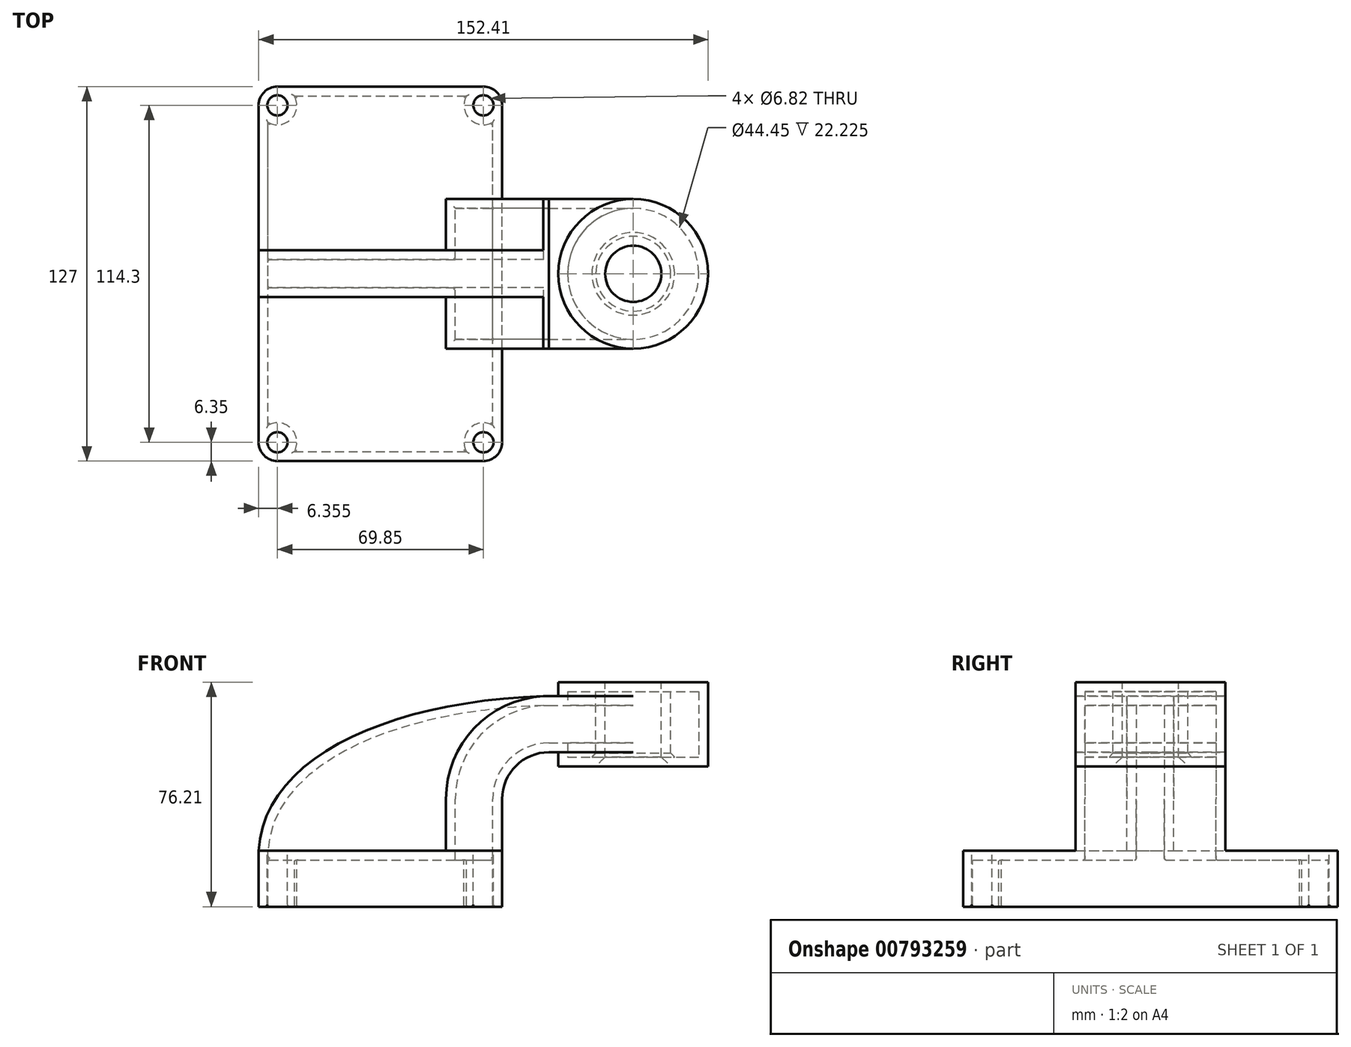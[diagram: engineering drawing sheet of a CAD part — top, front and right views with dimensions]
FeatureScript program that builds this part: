
annotation { "Feature Type Name" : "Feature", "Feature Type Description" : "" }
export const myFeature = defineFeature(function(context is Context, id is Id, definition is map)
    precondition{}
    {
        {
            var Q0;
            Q0=qCreatedBy(makeId("Front.planeOp"),FACE);
            var sketch = newSketch(context, id + "F0", { "sketchPlane" : qUnion([Q0])});
            skLineSegment(sketch, "E0.bottom", {"start": v(-41.28, -9.53) * mm, "end": v(41.28, -9.53) * mm});
            skLineSegment(sketch, "E0.top", {"start": v(-41.28, 9.53) * mm, "end": v(41.28, 9.53) * mm});
            skLineSegment(sketch, "E0.left", {"start": v(-41.28, -9.53) * mm, "end": v(-41.28, 9.53) * mm});
            skLineSegment(sketch, "E0.right", {"start": v(41.28, -9.53) * mm, "end": v(41.28, 9.53) * mm});
            skPoint(sketch, "E0.middle", {"position": v(0, 0) * mm});
            skLineSegment(sketch, "E1.bottom", {"start": v(60.32, 38.1) * mm, "end": v(111.12, 38.1) * mm});
            skLineSegment(sketch, "E1.top", {"start": v(60.32, 66.67) * mm, "end": v(111.12, 66.67) * mm});
            skLineSegment(sketch, "E1.left", {"start": v(60.32, 38.1) * mm, "end": v(60.32, 66.67) * mm});
            skLineSegment(sketch, "E1.right", {"start": v(111.12, 38.1) * mm, "end": v(111.12, 66.67) * mm});
            skPoint(sketch, "E1.middle", {"position": v(85.72, 52.39) * mm});
            skLineSegment(sketch, "E2", {"start": v(41.28, 9.53) * mm, "end": v(41.28, 27) * mm});
            skArc(sketch, "E3", {"start": v(41.27, 27) * mm, "mid": v(45.92, 38.23) * mm, "end": v(57.15, 42.88) * mm});
            skLineSegment(sketch, "E4", {"start": v(57.15, 42.88) * mm, "end": v(85.72, 42.88) * mm});
            skLineSegment(sketch, "E5.0", {"start": v(57.15, 61.93) * mm, "end": v(85.72, 61.93) * mm});
            skArc(sketch, "E5.1", {"start": v(22.22, 27) * mm, "mid": v(32.45, 51.7) * mm, "end": v(57.15, 61.93) * mm});
            skLineSegment(sketch, "E5.2", {"start": v(22.22, 9.53) * mm, "end": v(22.22, 27) * mm});
            skLineSegment(sketch, "E6", {"start": v(85.72, 38.1) * mm, "end": v(85.72, 66.67) * mm});
            skPoint(sketch, "E7.orphan", {"position": v(85.72, 42.88) * mm});
            skFitSpline(sketch, "E8", {"points": [v(-41.28, 9.53) * mm, v(57.15, 61.93) * mm], "startDerivative": vector(4.92, 96) * mm, "endDerivative": vector(159.26, 3.79) * mm});
            skSolve(sketch);
        }
        {
            var Q0;
            Q0=makeQuery(id+"F0.imprint","IMPRINT",FACE,{"disambiguationData":[TD([[makeQuery(id+"F0.imprint","IMPRINT",EDGE,{"derivedFrom":sQuery(id+"F0.wireOp",EDGE,"E0.bottom")}),1.0]])]});
            extrude(context, id + "F1", {"entities" : qUnion([Q0]), "depth" : 127 * mm, "offsetDistance" : 25.4 * mm, "symmetric" : true});
        }
        {
            var Q0;
            {var subQ1=sQuery(id+"F0.wireOp",EDGE,"E2");Q0=makeQuery(id+"F0.imprint","IMPRINT",FACE,{"disambiguationData":[TD([[makeQuery(id+"F0.imprint","IMPRINT",EDGE,{"derivedFrom":subQ1}),1.0]])]});}
            extrude(context, id + "F2", {"entities" : qUnion([Q0]), "operationType" : NewBodyOperationType.ADD, "depth" : 50.8 * mm, "offsetDistance" : 25.4 * mm, "symmetric" : true});
        }
        {
            var Q0;
            {var subQ3=sQuery(id+"F0.wireOp",EDGE,"E5.2");Q0=makeQuery(id+"F0.imprint","IMPRINT",FACE,{"disambiguationData":[TD([[makeQuery(id+"F0.imprint","IMPRINT",EDGE,{"derivedFrom":subQ3}),1.0]])]});}
            extrude(context, id + "F3", {"entities" : qUnion([Q0]), "operationType" : NewBodyOperationType.ADD, "depth" : 15.88 * mm, "offsetDistance" : 25.4 * mm, "symmetric" : true});
        }
        {
            var Q0;
            {var subQ0=sQuery(id+"F0.wireOp",EDGE,"E4");var subQ1=sQuery(id+"F0.wireOp",EDGE,"E1.left");var subQ2=makeQuery(id+"F0.imprint","INTERSECT",VERTEX,{"derivedFrom":[subQ1,subQ0]});Q0=makeQuery(id+"F0.imprint","IMPRINT",FACE,{"disambiguationData":[TD([[makeQuery(id+"F0.imprint","IMPRINT",EDGE,{"disambiguationData":[TD([[subQ2,-1.0]])],"derivedFrom":subQ1}),-1.0]])]});}
            extrude(context, id + "F4", {"entities" : qUnion([Q0]), "operationType" : NewBodyOperationType.ADD, "depth" : 50.8 * mm, "offsetDistance" : 25.4 * mm, "symmetric" : true});
        }
        {
            var Q0;
            {var subQ4=sQuery(id+"F0.wireOp",EDGE,"E1.right");Q0=makeQuery(id+"F0.imprint","IMPRINT",FACE,{"disambiguationData":[TD([[makeQuery(id+"F0.imprint","IMPRINT",EDGE,{"derivedFrom":subQ4}),1.0]])]});}
            var Q1;
            Q1=sQuery(id+"F0.wireOp",EDGE,"E6");
            revolve(context, id + "F5", {"operationType" : NewBodyOperationType.ADD, "surfaceOperationType" : NewSurfaceOperationType.NEW, "entities" : qUnion([Q0]), "axis" : qUnion([Q1]), "revolveType" : RevolveType.FULL});
        }
        {
            var Q0;
            Q0=makeQuery(id+"F1.opExtrude","CAP_EDGE",EDGE,{"disambiguationData":[OSD([sQuery(id+"F0.wireOp",EDGE,"E0.right")])],"isStart":false});
            var Q1;
            Q1=makeQuery(id+"F1.opExtrude","CAP_EDGE",EDGE,{"disambiguationData":[OSD([sQuery(id+"F0.wireOp",EDGE,"E0.left")])],"isStart":false});
            var Q2;
            Q2=makeQuery(id+"F1.opExtrude","CAP_EDGE",EDGE,{"disambiguationData":[OSD([sQuery(id+"F0.wireOp",EDGE,"E0.right")])],"isStart":true});
            var Q3;
            Q3=makeQuery(id+"F1.opExtrude","CAP_EDGE",EDGE,{"disambiguationData":[OSD([sQuery(id+"F0.wireOp",EDGE,"E0.left")])],"isStart":true});
            fillet(context, id + "F6", {"entities" : qUnion([Q0, Q1, Q2, Q3]), "radius" : 6.35 * mm, "tangentPropagation" : true, "allowEdgeOverflow" : false});
        }
        {
            var Q0;
            Q0=makeQuery(id+"F5.opRevolve","SWEPT_FACE",FACE,{"disambiguationData":[OSD([sQuery(id+"F0.wireOp",EDGE,"E1.top")])]});
            var sketch = newSketch(context, id + "F7", { "sketchPlane" : qUnion([Q0])});
            skCircle(sketch, "E9", {"center": v(85.72, 0) * mm, "radius": 9.53 * mm});
            skSolve(sketch);
        }
        {
            var Q0;
            Q0 = qSketchRegion(id + "F7", true);
            extrude(context, id + "F8", {"entities" : qUnion([Q0]), "operationType" : NewBodyOperationType.REMOVE, "endBound" : BoundingType.THROUGH_ALL, "oppositeDirection" : true, "depth" : 25.4 * mm, "offsetDistance" : 25.4 * mm});
        }
        {
            var Q0;
            Q0=makeQuery(id+"F8.boolean.opBoolean","COPY",EDGE,{"derivedFrom":makeQuery(id+"F8.opExtrude","CAP_EDGE",EDGE,{"disambiguationData":[OSD([sQuery(id+"F7.wireOp",EDGE,"E9")])],"isStart":true})});
            var Q1;
            Q1=makeQuery(id+"F8.boolean.opBoolean","INTERSECT",EDGE,{"derivedFrom":[makeQuery(id+"F5.opRevolve","SWEPT_FACE",FACE,{"disambiguationData":[OSD([sQuery(id+"F0.wireOp",EDGE,"E1.bottom")])]}),makeQuery(id+"F8.opExtrude","SWEPT_FACE",FACE,{"disambiguationData":[OSD([sQuery(id+"F7.wireOp",EDGE,"E9")])]})]});
            chamfer(context, id + "F9", {"entities" : qUnion([Q0, Q1]), "width" : 3.17 * mm, "tangentPropagation" : true});
        }
        {
            var Q0;
            {var subQ4=sQuery(id+"F0.wireOp",EDGE,"E0.top");var subQ5=sQuery(id+"F0.wireOp",EDGE,"E0.right");var subQ6=sQuery(id+"F0.wireOp",EDGE,"E0.left");Q0=makeQuery(id+"F3.boolean.opBoolean","SPLIT",FACE,{"disambiguationData":[TD([makeQuery(id+"F1.opExtrude","CAP_FACE",FACE,{"disambiguationData":[OSD([sQuery(id+"F0.wireOp",EDGE,"E0.bottom"),subQ4,subQ6,subQ5])],"isStart":false})])],"derivedFrom":makeQuery(id+"F1.opExtrude","SWEPT_FACE",FACE,{"disambiguationData":[OSD([subQ4])]})});}
            var sketch = newSketch(context, id + "F10", { "sketchPlane" : qUnion([Q0])});
            skCircle(sketch, "E10", {"center": v(-34.93, -57.15) * mm, "radius": 3.41 * mm});
            skCircle(sketch, "E11.MirrorC", {"center": v(34.93, -57.15) * mm, "radius": 3.41 * mm});
            skCircle(sketch, "E12.MirrorC", {"center": v(-34.93, 57.15) * mm, "radius": 3.41 * mm});
            skCircle(sketch, "E13.MirrorC", {"center": v(34.93, 57.15) * mm, "radius": 3.41 * mm});
            skSolve(sketch);
        }
        {
            var Q0;
            Q0 = qSketchRegion(id + "F10", true);
            extrude(context, id + "F11", {"entities" : qUnion([Q0]), "operationType" : NewBodyOperationType.REMOVE, "endBound" : BoundingType.THROUGH_ALL, "oppositeDirection" : true, "depth" : 25.4 * mm, "offsetDistance" : 25.4 * mm});
        }
        {
            var Q0;
            Q0=makeQuery(id+"F11.boolean.opBoolean","COPY",EDGE,{"derivedFrom":makeQuery(id+"F11.opExtrude","CAP_EDGE",EDGE,{"disambiguationData":[OSD([sQuery(id+"F10.wireOp",EDGE,"E10")])],"isStart":true})});
            var Q1;
            Q1=makeQuery(id+"F11.boolean.opBoolean","COPY",EDGE,{"derivedFrom":makeQuery(id+"F11.opExtrude","CAP_EDGE",EDGE,{"disambiguationData":[OSD([sQuery(id+"F10.wireOp",EDGE,"E12.MirrorC")])],"isStart":true})});
            var Q2;
            Q2=makeQuery(id+"F11.boolean.opBoolean","COPY",EDGE,{"derivedFrom":makeQuery(id+"F11.opExtrude","CAP_EDGE",EDGE,{"disambiguationData":[OSD([sQuery(id+"F10.wireOp",EDGE,"E13.MirrorC")])],"isStart":true})});
            var Q3;
            Q3=makeQuery(id+"F11.boolean.opBoolean","COPY",EDGE,{"derivedFrom":makeQuery(id+"F11.opExtrude","CAP_EDGE",EDGE,{"disambiguationData":[OSD([sQuery(id+"F10.wireOp",EDGE,"E11.MirrorC")])],"isStart":true})});
            var Q4;
            Q4=makeQuery(id+"F11.boolean.opBoolean","INTERSECT",EDGE,{"derivedFrom":[makeQuery(id+"F1.opExtrude","SWEPT_FACE",FACE,{"disambiguationData":[OSD([sQuery(id+"F0.wireOp",EDGE,"E0.bottom")])]}),makeQuery(id+"F11.opExtrude","SWEPT_FACE",FACE,{"disambiguationData":[OSD([sQuery(id+"F10.wireOp",EDGE,"E12.MirrorC")])]})]});
            var Q5;
            Q5=makeQuery(id+"F11.boolean.opBoolean","INTERSECT",EDGE,{"derivedFrom":[makeQuery(id+"F1.opExtrude","SWEPT_FACE",FACE,{"disambiguationData":[OSD([sQuery(id+"F0.wireOp",EDGE,"E0.bottom")])]}),makeQuery(id+"F11.opExtrude","SWEPT_FACE",FACE,{"disambiguationData":[OSD([sQuery(id+"F10.wireOp",EDGE,"E10")])]})]});
            var Q6;
            Q6=makeQuery(id+"F11.boolean.opBoolean","INTERSECT",EDGE,{"derivedFrom":[makeQuery(id+"F1.opExtrude","SWEPT_FACE",FACE,{"disambiguationData":[OSD([sQuery(id+"F0.wireOp",EDGE,"E0.bottom")])]}),makeQuery(id+"F11.opExtrude","SWEPT_FACE",FACE,{"disambiguationData":[OSD([sQuery(id+"F10.wireOp",EDGE,"E13.MirrorC")])]})]});
            var Q7;
            Q7=makeQuery(id+"F11.boolean.opBoolean","INTERSECT",EDGE,{"derivedFrom":[makeQuery(id+"F1.opExtrude","SWEPT_FACE",FACE,{"disambiguationData":[OSD([sQuery(id+"F0.wireOp",EDGE,"E0.bottom")])]}),makeQuery(id+"F11.opExtrude","SWEPT_FACE",FACE,{"disambiguationData":[OSD([sQuery(id+"F10.wireOp",EDGE,"E11.MirrorC")])]})]});
            fillet(context, id + "F12", {"entities" : qUnion([Q0, Q1, Q2, Q3, Q4, Q5, Q6, Q7]), "radius" : 0.76 * mm, "tangentPropagation" : true, "allowEdgeOverflow" : false});
        }
        {
            var Q0;
            Q0=makeQuery(id+"F1.opExtrude","SWEPT_FACE",FACE,{"disambiguationData":[OSD([sQuery(id+"F0.wireOp",EDGE,"E0.bottom")])]});
            shell(context, id + "F13", {"entities" : qUnion([Q0]), "thickness" : 3.17 * mm});
        }
        {
            var Q0;
            {var subQ0=sQuery(id+"F0.wireOp",EDGE,"E0.bottom");Q0=makeQuery(id+"F13.opShell","OFFSET_EDGE",EDGE,{"disambiguationData":[OSD([subQ0]),TDD([makeQuery(id+"F1.opExtrude","CAP_EDGE",EDGE,{"disambiguationData":[OSD([subQ0])],"isStart":false})])]});}
            var Q1;
            Q1=makeQuery(id+"F13.opShell","OFFSET_EDGE",EDGE,{"disambiguationData":[OSD([sQuery(id+"F0.wireOp",EDGE,"E0.bottom"),sQuery(id+"F10.wireOp",EDGE,"E11.MirrorC")])]});
            var Q2;
            Q2=makeQuery(id+"F13.opShell","OFFSET_EDGE",EDGE,{"disambiguationData":[OSD([sQuery(id+"F0.wireOp",EDGE,"E0.bottom"),sQuery(id+"F0.wireOp",EDGE,"E0.right")])]});
            var Q3;
            Q3=makeQuery(id+"F13.opShell","OFFSET_EDGE",EDGE,{"disambiguationData":[OSD([sQuery(id+"F0.wireOp",EDGE,"E0.bottom"),sQuery(id+"F10.wireOp",EDGE,"E13.MirrorC")])]});
            var Q4;
            {var subQ0=sQuery(id+"F0.wireOp",EDGE,"E0.bottom");Q4=makeQuery(id+"F13.opShell","OFFSET_EDGE",EDGE,{"disambiguationData":[OSD([subQ0]),TDD([makeQuery(id+"F1.opExtrude","CAP_EDGE",EDGE,{"disambiguationData":[OSD([subQ0])],"isStart":true})])]});}
            var Q5;
            Q5=makeQuery(id+"F13.opShell","OFFSET_EDGE",EDGE,{"disambiguationData":[OSD([sQuery(id+"F0.wireOp",EDGE,"E0.bottom"),sQuery(id+"F10.wireOp",EDGE,"E12.MirrorC")])]});
            var Q6;
            Q6=makeQuery(id+"F13.opShell","OFFSET_EDGE",EDGE,{"disambiguationData":[OSD([sQuery(id+"F0.wireOp",EDGE,"E0.bottom"),sQuery(id+"F0.wireOp",EDGE,"E0.left")])]});
            var Q7;
            Q7=makeQuery(id+"F13.opShell","OFFSET_EDGE",EDGE,{"disambiguationData":[OSD([sQuery(id+"F0.wireOp",EDGE,"E0.bottom"),sQuery(id+"F10.wireOp",EDGE,"E10")])]});
            var Q8;
            {var subQ4=sQuery(id+"F0.wireOp",EDGE,"E0.top");var subQ5=sQuery(id+"F0.wireOp",EDGE,"E0.right");var subQ6=sQuery(id+"F0.wireOp",EDGE,"E0.left");Q8=makeQuery(id+"F13.opShell","OFFSET_FACE",FACE,{"disambiguationData":[OSD([subQ4]),TDD([makeQuery(id+"F3.boolean.opBoolean","SPLIT",FACE,{"disambiguationData":[TD([makeQuery(id+"F1.opExtrude","CAP_FACE",FACE,{"disambiguationData":[OSD([sQuery(id+"F0.wireOp",EDGE,"E0.bottom"),subQ4,subQ6,subQ5])],"isStart":false})])],"derivedFrom":makeQuery(id+"F1.opExtrude","SWEPT_FACE",FACE,{"disambiguationData":[OSD([subQ4])]})})])]});}
            var Q9;
            {var subQ4=sQuery(id+"F0.wireOp",EDGE,"E0.top");var subQ5=sQuery(id+"F0.wireOp",EDGE,"E0.right");var subQ6=sQuery(id+"F0.wireOp",EDGE,"E0.left");Q9=makeQuery(id+"F13.opShell","OFFSET_FACE",FACE,{"disambiguationData":[OSD([subQ4]),TDD([makeQuery(id+"F3.boolean.opBoolean","SPLIT",FACE,{"disambiguationData":[TD([makeQuery(id+"F1.opExtrude","CAP_FACE",FACE,{"disambiguationData":[OSD([sQuery(id+"F0.wireOp",EDGE,"E0.bottom"),subQ4,subQ6,subQ5])],"isStart":true})])],"derivedFrom":makeQuery(id+"F1.opExtrude","SWEPT_FACE",FACE,{"disambiguationData":[OSD([subQ4])]})})])]});}
            fillet(context, id + "F14", {"entities" : qUnion([Q0, Q1, Q2, Q3, Q4, Q5, Q6, Q7, Q8, Q9]), "radius" : 0.5 * mm, "tangentPropagation" : true, "allowEdgeOverflow" : false});
        }
    });
